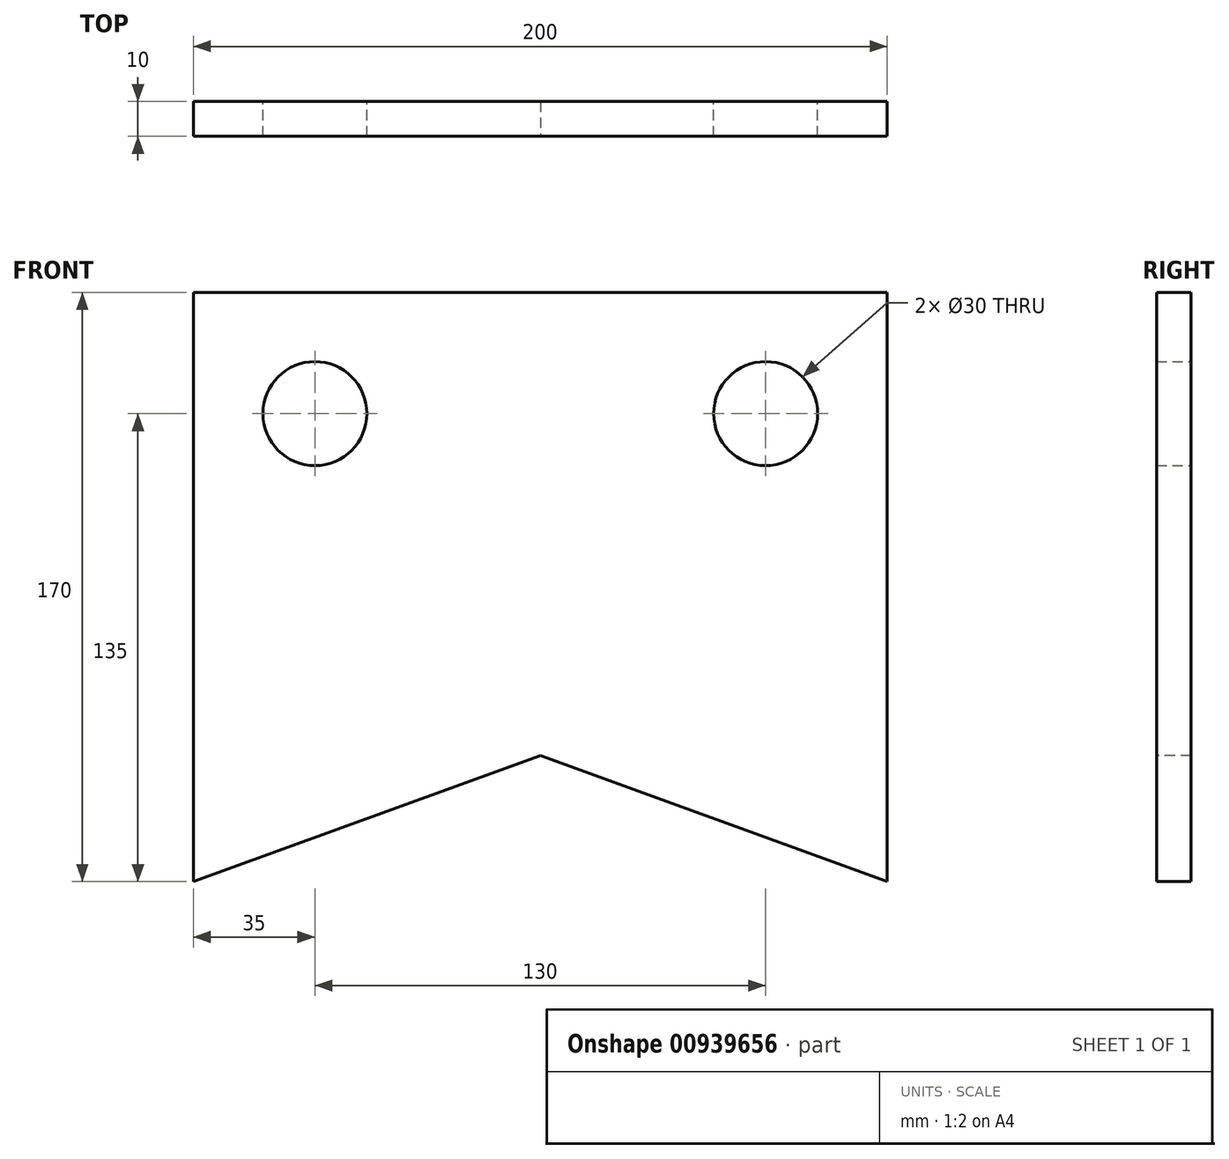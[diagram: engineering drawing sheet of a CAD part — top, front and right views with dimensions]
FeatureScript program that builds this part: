
annotation { "Feature Type Name" : "Feature", "Feature Type Description" : "" }
export const myFeature = defineFeature(function(context is Context, id is Id, definition is map)
    precondition{}
    {
        {
            var Q0;
            Q0=qCreatedBy(makeId("Front.planeOp"),FACE);
            var sketch = newSketch(context, id + "F0", { "sketchPlane" : qUnion([Q0])});
            skLineSegment(sketch, "E0.bottom", {"start": v(100, -85) * mm, "end": v(-100, -85) * mm});
            skLineSegment(sketch, "E0.top", {"start": v(100, 85) * mm, "end": v(-100, 85) * mm});
            skLineSegment(sketch, "E0.left", {"start": v(100, -85) * mm, "end": v(100, 85) * mm});
            skLineSegment(sketch, "E0.right", {"start": v(-100, -85) * mm, "end": v(-100, 85) * mm});
            skPoint(sketch, "E0.middle", {"position": v(0, 0) * mm});
            skCircle(sketch, "E1", {"center": v(65, 50) * mm, "radius": 15 * mm});
            skCircle(sketch, "E2.MirrorC", {"center": v(-65, 50) * mm, "radius": 15 * mm});
            skSolve(sketch);
        }
        {
            var Q0;
            Q0 = qSketchRegion(id + "F0", true);
            extrude(context, id + "F1", {"entities" : qUnion([Q0]), "depth" : 10 * mm, "offsetDistance" : 25 * mm});
        }
        {
            var Q0;
            Q0=makeQuery(id+"F1.opExtrude","CAP_FACE",FACE,{"disambiguationData":[OSD([sQuery(id+"F0.wireOp",EDGE,"E0.bottom"),sQuery(id+"F0.wireOp",EDGE,"E0.top"),sQuery(id+"F0.wireOp",EDGE,"E0.left"),sQuery(id+"F0.wireOp",EDGE,"E0.right"),sQuery(id+"F0.wireOp",EDGE,"E1"),sQuery(id+"F0.wireOp",EDGE,"E2.MirrorC")])],"isStart":false});
            var sketch = newSketch(context, id + "F2", { "sketchPlane" : qUnion([Q0])});
            skLineSegment(sketch, "E3", {"start": v(-100, -85) * mm, "end": v(0, -48.6) * mm});
            skLineSegment(sketch, "E4", {"start": v(0, -48.6) * mm, "end": v(100, -85) * mm});
            skSolve(sketch);
        }
        {
            var Q0;
            Q0 = qSketchRegion(id + "F2", true);
            var Q1;
            Q1=makeQuery(id+"F2.imprint","IMPRINT",FACE,{"disambiguationData":[TD([[makeQuery(id+"F2.imprint","IMPRINT",EDGE,{"derivedFrom":sQuery(id+"F2.wireOp",EDGE,"E3")}),-1.0]])]});
            extrude(context, id + "F3", {"entities" : qUnion([Q0, Q1]), "operationType" : NewBodyOperationType.REMOVE, "endBound" : BoundingType.THROUGH_ALL, "oppositeDirection" : true, "depth" : 25 * mm, "offsetDistance" : 25 * mm});
        }
    });
